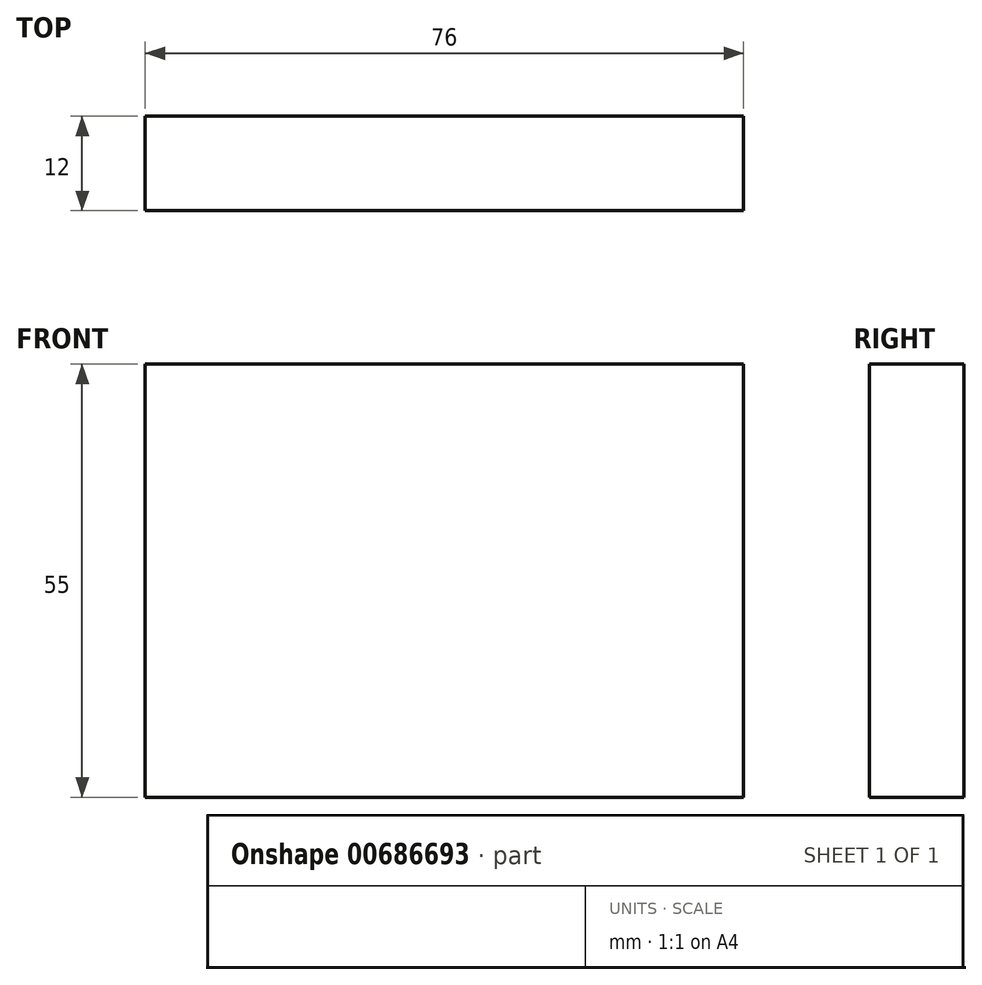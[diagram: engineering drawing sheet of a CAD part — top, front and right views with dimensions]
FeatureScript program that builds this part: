
annotation { "Feature Type Name" : "Feature", "Feature Type Description" : "" }
export const myFeature = defineFeature(function(context is Context, id is Id, definition is map)
    precondition{}
    {
        {
            var Q0;
            Q0=qCreatedBy(makeId("Front.planeOp"),FACE);
            var sketch = newSketch(context, id + "F0", { "sketchPlane" : qUnion([Q0])});
            skLineSegment(sketch, "E0.bottom", {"start": v(0, 0) * mm, "end": v(76, 0) * mm});
            skLineSegment(sketch, "E0.top", {"start": v(0, 55) * mm, "end": v(76, 55) * mm});
            skLineSegment(sketch, "E0.left", {"start": v(0, 0) * mm, "end": v(0, 55) * mm});
            skLineSegment(sketch, "E0.right", {"start": v(76, 0) * mm, "end": v(76, 55) * mm});
            skSolve(sketch);
        }
        {
            var Q0;
            Q0=qSketchRegion(id+"F0",true);
            extrude(context, id + "F1", {"entities" : qUnion([Q0]), "depth" : 12 * mm, "offsetDistance" : 25 * mm});
        }
    });
